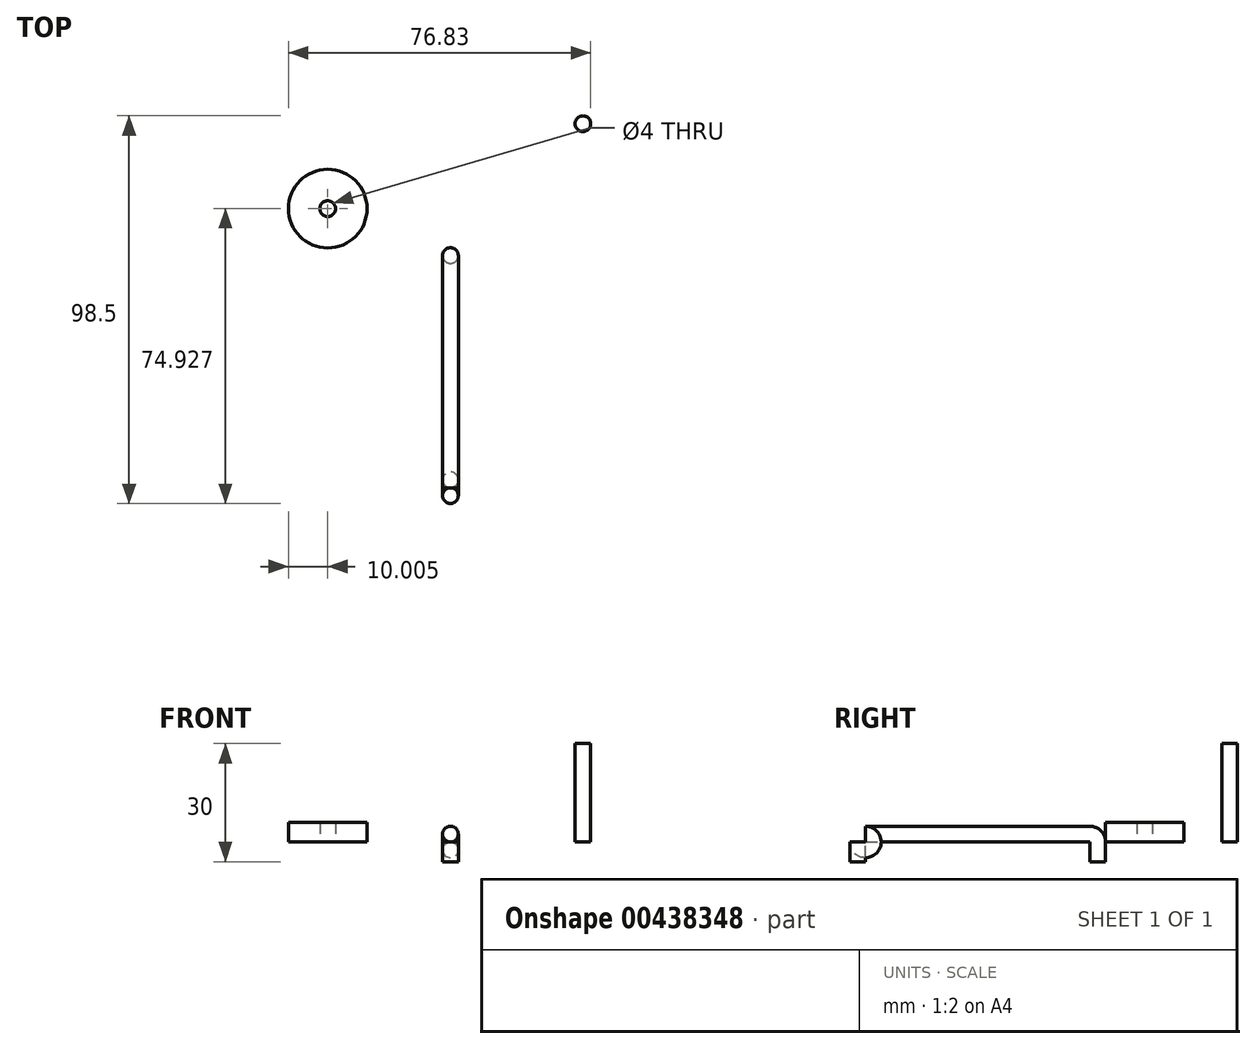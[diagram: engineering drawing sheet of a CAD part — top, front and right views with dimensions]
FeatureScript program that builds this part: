
annotation { "Feature Type Name" : "Feature", "Feature Type Description" : "" }
export const myFeature = defineFeature(function(context is Context, id is Id, definition is map)
    precondition{}
    {
        {
            var Q0;
            Q0=qCreatedBy(makeId("Top.planeOp"),FACE);
            var sketch = newSketch(context, id + "F0", { "sketchPlane" : qUnion([Q0])});
            skCircle(sketch, "E0", {"center": v(0, 0) * mm, "radius": 2 * mm});
            skLineSegment(sketch, "E1", {"start": v(0, -2) * mm, "end": v(-10.96, -2) * mm});
            skSolve(sketch);
        }
        {
            var Q0;
            Q0 = qSketchRegion(id + "F0", true);
            var Q1;
            Q1=sQuery(id+"F0.wireOp",EDGE,"E1");
            revolve(context, id + "F1", {"entities" : qUnion([Q0]), "axis" : qUnion([Q1]), "revolveType" : RevolveType.ONE_DIRECTION, "oppositeDirection" : true, "angle" : 90 * degree});
        }
        {
            var Q0;
            Q0=makeQuery(id+"F1.opRevolve","CAP_FACE",FACE,{"disambiguationData":[OSD([sQuery(id+"F0.wireOp",EDGE,"E0")])],"isStart":false});
            extrude(context, id + "F2", {"entities" : qUnion([Q0]), "operationType" : NewBodyOperationType.ADD, "depth" : 57 * mm});
        }
        {
            var Q0;
            Q0=makeQuery(id+"F2.opExtrude","CAP_FACE",FACE,{"disambiguationData":[OSD([sQuery(id+"F0.wireOp",EDGE,"E0")])],"isStart":false});
            var sketch = newSketch(context, id + "F3", { "sketchPlane" : qUnion([Q0])});
            skLineSegment(sketch, "E2", {"start": v(0, 0) * mm, "end": v(-4.03, 0) * mm});
            skSolve(sketch);
        }
        {
            var Q0;
            Q0=makeQuery(id+"F3.imprint","IMPRINT",FACE,{"disambiguationData":[TD([[makeQuery(id+"F3.imprint","IMPRINT",EDGE,{"derivedFrom":makeQuery(id+"F2.opExtrude","CAP_EDGE",EDGE,{"disambiguationData":[OSD([sQuery(id+"F0.wireOp",EDGE,"E0")])],"isStart":false})}),1.0]])]});
            var Q1;
            Q1=sQuery(id+"F3.wireOp",EDGE,"E2");
            revolve(context, id + "F4", {"operationType" : NewBodyOperationType.ADD, "entities" : qUnion([Q0]), "axis" : qUnion([Q1]), "revolveType" : RevolveType.ONE_DIRECTION, "oppositeDirection" : true, "angle" : 90 * degree});
        }
        {
            var Q0;
            Q0=makeQuery(id+"F0.imprint","IMPRINT",FACE,{"disambiguationData":[TD([[makeQuery(id+"F0.imprint","IMPRINT",EDGE,{"derivedFrom":sQuery(id+"F0.wireOp",EDGE,"E0")}),1.0]])]});
            extrude(context, id + "F5", {"entities" : qUnion([Q0]), "operationType" : NewBodyOperationType.ADD, "oppositeDirection" : true, "depth" : 5 * mm});
        }
        {
            var Q0;
            Q0=makeQuery(id+"F4.opRevolve","CAP_FACE",FACE,{"disambiguationData":[OSD([sQuery(id+"F0.wireOp",EDGE,"E0")])],"isStart":false});
            extrude(context, id + "F6", {"entities" : qUnion([Q0]), "operationType" : NewBodyOperationType.ADD, "depth" : 5 * mm});
        }
        {
            var Q0;
            Q0=qCreatedBy(makeId("Top.planeOp"),FACE);
            var sketch = newSketch(context, id + "F7", { "sketchPlane" : qUnion([Q0])});
            skCircle(sketch, "E3", {"center": v(33.64, 33.5) * mm, "radius": 2 * mm});
            skSolve(sketch);
        }
        {
            var Q0;
            Q0 = qSketchRegion(id + "F7", true);
            extrude(context, id + "F8", {"entities" : qUnion([Q0]), "depth" : 25 * mm});
        }
        {
            var Q0;
            Q0=qCreatedBy(makeId("Top.planeOp"),FACE);
            var sketch = newSketch(context, id + "F9", { "sketchPlane" : qUnion([Q0])});
            skCircle(sketch, "E4", {"center": v(-31.19, 11.93) * mm, "radius": 10 * mm});
            skCircle(sketch, "E5", {"center": v(-31.19, 11.93) * mm, "radius": 2 * mm});
            skSolve(sketch);
        }
        {
            var Q0;
            Q0=makeQuery(id+"F9.imprint","IMPRINT",FACE,{"disambiguationData":[TD([[makeQuery(id+"F9.imprint","IMPRINT",EDGE,{"derivedFrom":sQuery(id+"F9.wireOp",EDGE,"E4")}),1.0]])]});
            extrude(context, id + "F10", {"entities" : qUnion([Q0]), "depth" : 5 * mm});
        }
    });
